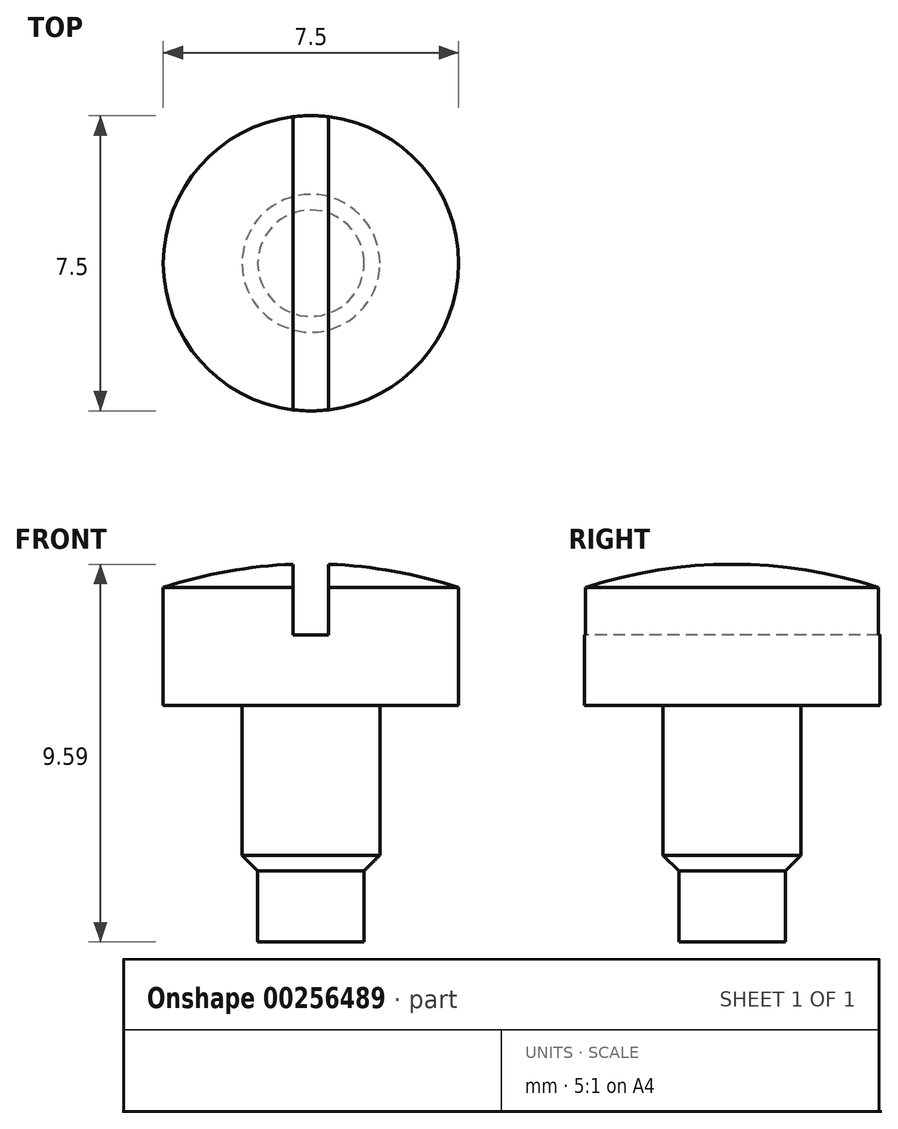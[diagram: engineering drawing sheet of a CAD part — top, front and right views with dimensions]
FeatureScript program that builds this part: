
annotation { "Feature Type Name" : "Feature", "Feature Type Description" : "" }
export const myFeature = defineFeature(function(context is Context, id is Id, definition is map)
    precondition{}
    {
        {
            var Q0;
            Q0=qCreatedBy(makeId("Front.planeOp"),FACE);
            var sketch = newSketch(context, id + "F0", { "sketchPlane" : qUnion([Q0])});
            skLineSegment(sketch, "E0", {"start": v(0, 0) * mm, "end": v(0.45, 0) * mm});
            skLineSegment(sketch, "E1", {"start": v(0.45, 0) * mm, "end": v(0.45, 0.6) * mm});
            skLineSegment(sketch, "E2", {"start": v(0.45, 0.6) * mm, "end": v(0.58, 0.73) * mm});
            skLineSegment(sketch, "E3", {"start": v(0.58, 0.73) * mm, "end": v(0.58, 2) * mm});
            skLineSegment(sketch, "E4", {"start": v(0.58, 2) * mm, "end": v(1.25, 2) * mm});
            skLineSegment(sketch, "E5", {"start": v(1.25, 2) * mm, "end": v(1.25, 3) * mm});
            skLineSegment(sketch, "E6", {"start": v(1.25, 3) * mm, "end": v(0, 3) * mm});
            skLineSegment(sketch, "E7", {"start": v(0, 3) * mm, "end": v(0, 0) * mm});
            skArc(sketch, "E8", {"start": v(1.25, 3) * mm, "mid": v(0.63, 3.15) * mm, "end": v(0, 3.2) * mm});
            skLineSegment(sketch, "E9", {"start": v(0, 3.2) * mm, "end": v(0, 3) * mm});
            skSolve(sketch);
        }
        {
            var Q0;
            {var subQ0=makeQuery(id+"F0.imprint","IMPRINT",EDGE,{"derivedFrom":sQuery(id+"F0.wireOp",EDGE,"E6")});Q0=qUnion([makeQuery(id+"F0.imprint","IMPRINT",FACE,{"disambiguationData":[TD([[makeQuery(id+"F0.imprint","IMPRINT",EDGE,{"derivedFrom":sQuery(id+"F0.wireOp",EDGE,"E0")}),1.0]])]}),makeQuery(id+"F0.imprint","IMPRINT",FACE,{"disambiguationData":[TD([[subQ0,-1.0]])]})]);}
            var Q1;
            Q1=sQuery(id+"F0.wireOp",EDGE,"E7");
            revolve(context, id + "F1", {"entities" : qUnion([Q0]), "axis" : qUnion([Q1]), "revolveType" : RevolveType.FULL});
        }
        {
            var Q0;
            Q0=qCreatedBy(makeId("Front.planeOp"),FACE);
            var sketch = newSketch(context, id + "F2", { "sketchPlane" : qUnion([Q0])});
            skLineSegment(sketch, "E10", {"start": v(-0.15, 2.6) * mm, "end": v(0.15, 2.6) * mm});
            skPoint(sketch, "E11", {"position": v(0, 2.6) * mm});
            skLineSegment(sketch, "E12", {"start": v(-0.15, 2.6) * mm, "end": v(-0.15, 3.25) * mm});
            skLineSegment(sketch, "E13", {"start": v(-0.15, 3.25) * mm, "end": v(0.15, 3.25) * mm});
            skLineSegment(sketch, "E14", {"start": v(0.15, 3.25) * mm, "end": v(0.15, 2.6) * mm});
            skSolve(sketch);
        }
        {
            var Q0;
            Q0=makeQuery(id+"F2.imprint","IMPRINT",FACE,{"disambiguationData":[TD([[makeQuery(id+"F2.imprint","IMPRINT",EDGE,{"derivedFrom":sQuery(id+"F2.wireOp",EDGE,"E10")}),1.0]])]});
            extrude(context, id + "F3", {"entities" : qUnion([Q0]), "operationType" : NewBodyOperationType.REMOVE, "oppositeDirection" : true, "depth" : 25 * mm, "symmetric" : true});
        }
        {
            var Q0;
            Q0=makeQuery(id+"F1.opRevolve","SWEPT_BODY",BODY,{"disambiguationData":[OSD([sQuery(id+"F0.wireOp",EDGE,"E0"),sQuery(id+"F0.wireOp",EDGE,"E1"),sQuery(id+"F0.wireOp",EDGE,"E2"),sQuery(id+"F0.wireOp",EDGE,"E3"),sQuery(id+"F0.wireOp",EDGE,"E4"),sQuery(id+"F0.wireOp",EDGE,"E5"),sQuery(id+"F0.wireOp",EDGE,"E7"),sQuery(id+"F0.wireOp",EDGE,"E8"),sQuery(id+"F0.wireOp",EDGE,"E9")])]});
            var Q1;
            Q1=qCreatedBy(makeId("Origin.pointOp"),VERTEX);
            transform(context, id + "F4", {"entities" : qUnion([Q0]), "transformType" : TransformType.SCALE_UNIFORMLY, "scale" : 3, "makeCopy" : false, "scalePoint" : qUnion([Q1])});
        }
    });
